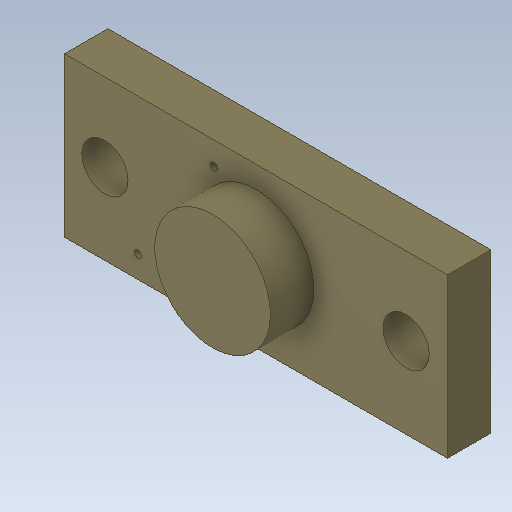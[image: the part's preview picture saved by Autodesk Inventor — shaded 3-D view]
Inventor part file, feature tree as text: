
AUTODESK INVENTOR PART (.ipt)
format: ipt  version: 2020 (Build 240168000, 168)  size: 134,144 bytes
history: mixed  units: in
note: dims shown in document units (in); Inventor stores cm internally (conversion verified against a paired STEP export)
features: other x1, extrude x1, sketch x1, projected_geometry x1, imported_body x1
ambient origin geometry x8: Origin, YZ Plane, XZ Plane, XY Plane, X Axis, Y Axis, Z Axis, Center Point
bodies: Solid1 (imported_parasolid)
feature tree (5):
  other  "Board"
  extrude  "Extrusion1"  Depth=0.0591in TaperAngle=0.0deg
  sketch  "Sketch1"  dims[d0=0.1575in d1=0.0591in d2=0.0in]
  projected_geometry  "Projected Loop1"
  imported_body  NMx_Import_Brep_tag  [imported B-rep: ~18 faces, bbox_mm=[13.238, 5.492, 3.0]]
